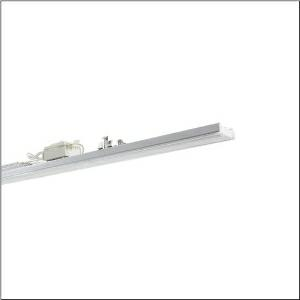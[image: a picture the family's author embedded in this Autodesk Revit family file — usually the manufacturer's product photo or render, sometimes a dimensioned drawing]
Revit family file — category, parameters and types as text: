
# Revit family: licross_r__11_recessed_mo_51tl12mn4axg_4b25
name_source: partatom
category: Lighting Fixtures
units: mm (PartAtom-declared; Revit-internal decimal feet)

## family parameters
Cut with Voids When Loaded = No
Host = Face
Light Source = No
Part Type = Normal
Room Calculation Point = No
Round Connector Dimension = Use Diameter
Shared = No

## types (1)
- --- (1 x LED, 10290 lm, 55.2 W, 4000K)
    Apparent Load = 55 VA
    CIE Flux Codes = 67 92 99 100 100
    Color Rendering = 80
    Color Temperature = 4000K
    Default Elevation = 1800 mm
    Description = Licross® 11 Recessed MO, luminaire insert, of sheet steel, coil coated, white, length: 1.500mm, width: 66mm, height: 67mm, LED rated luminous flux: 10.290lm, light colour: 840, control gear: ON/OFF Multilumen, with plug, 3-pole, with phase selection, mains connection: 220..240V, AC, 50/60Hz, rated input power: 55W, internal wiring halogen-free, primary optical cover: cover, of PMMA, light emission: direct distribution, primary light characteristic: symmetric, protection rating (complete): IP40, insulation class (complete): insulation class I (protective earthing), certification: CE, ENEC, VDE, UKCA, protection symbol: D if used in an environment without relevant dust loads with corresponding accessories, impact resistance: IK06, permissible ambient temperature for indoor applications: -35..+40°C, corresponds to IFS (International Featured Standards) requirements for safety and quality in the food industry, reducing of maximum allowable ambient temperature of 5°C with ceiling mounting, packaging unit: 1 piece
    Height = 58 mm
    Lamp = 1 x LED
    Lamp Light Flux = 10290 lm
    Lamp Power = 55.2 W
    Lamp count = 1
    Length = 1500 mm
    Luminous efficacy = 186 lm/W
    Manufacturer = Siteco
    ModVariant = No
    Model = 51TL12MN4AXG
    Mounting Place = Ceiling
    Mounting Type = Pendant
    Number of Poles = 1
    OnlyDefault = Yes
    Power Factor = 1
    Product Name = Licross® 11 Recessed MO
    Product group = luminaire insert | ceiling pendant
    ProductGroupID = 902
    Protection Class = Protection class I
    Protection Degree = IP 40
    RLX_Detail_Level = 1
    RLX_Emergency_Light_Flux = 0 lm
    RLX_Emergency_Type = 0
    RLX_Emergency_Type_DB = No
    RlxData = <blob elided: 22129 chars, md5=99d27cac>
    Socket = socket
    Standby Power = 0 W
    System Light Flux = 10290 lm
    System Power = 55 W
    Type Comments = factory setting: luminous flux: 100 % | (A | C | E) | 126 mA
    Type Image = l_1296930.jpg
    URL = http://relux.com
    VarID = @adj_107109
    Voltage = 0 V
    Weight = 0.00 kg
    Width = 66 mm

## geometry (parser evidence)
native form markers: Blend x4, Sweep x11
no freeform markers — native parametric forms only
